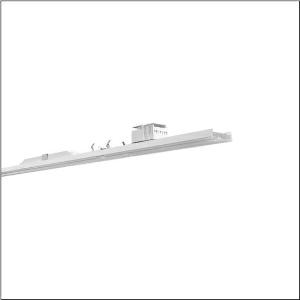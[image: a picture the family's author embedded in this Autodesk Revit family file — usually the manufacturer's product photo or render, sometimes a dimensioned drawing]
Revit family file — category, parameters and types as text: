
# Revit family: licross_r__21_recessed_mo_52tl12dnd75f_9c15
name_source: partatom
category: Lighting Fixtures
units: mm (PartAtom-declared; Revit-internal decimal feet)

## family parameters
Cut with Voids When Loaded = No
Host = Face
Light Source = No
Part Type = Normal
Room Calculation Point = No
Round Connector Dimension = Use Diameter
Shared = No

## types (1)
- --- (1 x LED, 7960 lm, 61.1 W, 4000K)
    Apparent Load = 61 VA
    CIE Flux Codes = 72 92 99 100 100
    Color Rendering = 90
    Color Temperature = 4000K
    Default Elevation = 1800 mm
    Description = Licross® 21 Recessed MO, luminaire insert, of sheet steel, galvanised, coil coated, white, length: 1.500mm, width: 66mm, height: 67mm, LED rated luminous flux: 7.960lm, light colour: 940, control gear: DALI 2, control gear: ECG DALI, with plug, 5-pole, with phase selection, mains connection: 220..240V, AC, 50/60Hz, rated input power: 61W, halogen-free wiring, primary optical cover: cover, of PMMA, light emission: direct distribution, primary light characteristic: symmetric, protection rating (complete): IP40, insulation class (complete): insulation class I (protective earthing), certification: CE, ENEC, VDE, UKCA, protection symbol: D if used in an environment without relevant dust loads with corresponding accessories, impact resistance: IK06, permissible ambient temperature for indoor applications: -25..+35°C, corresponds to IFS (International Featured Standards) requirements for safety and quality in the food industry, reducing of maximum allowable ambient temperature of 5°C with ceiling mounting, LABS conformity tested according to VDMA 24364:2018-05, packaging unit: 1 piece
    Height = 58 mm
    Lamp = 1 x LED
    Lamp Light Flux = 7960 lm
    Lamp Power = 61.1 W
    Lamp count = 1
    Length = 1500 mm
    Luminous efficacy = 130 lm/W
    Manufacturer = Siteco
    ModVariant = No
    Model = 52TL12DND75F
    Mounting Place = Ceiling
    Mounting Type = Pendant
    Number of Poles = 1
    OnlyDefault = Yes
    Power Factor = 1
    Product Name = Licross® 21 Recessed MO
    Product group = luminaire insert
    ProductGroupID = 901
    Protection Class = Protection class I
    Protection Degree = IP 40
    RLX_Detail_Level = 1
    RLX_Emergency_Light_Flux = 0 lm
    RLX_Emergency_Type = 0
    RLX_Emergency_Type_DB = No
    RlxData = <blob elided: 22621 chars, md5=52298ad2>
    Socket = socket
    Standby Power = 0 W
    System Light Flux = 7960 lm
    System Power = 61 W
    Type Comments = factory setting: luminous flux: 100 % | dim-lin: 254 | 405 mA
    Type Image = l_1296935.jpg
    URL = http://relux.com
    VarID = @adj_135897
    Voltage = 0 V
    Weight = 0.00 kg
    Width = 66 mm

## geometry (parser evidence)
native form markers: Blend x4, Sweep x12
no freeform markers — native parametric forms only
